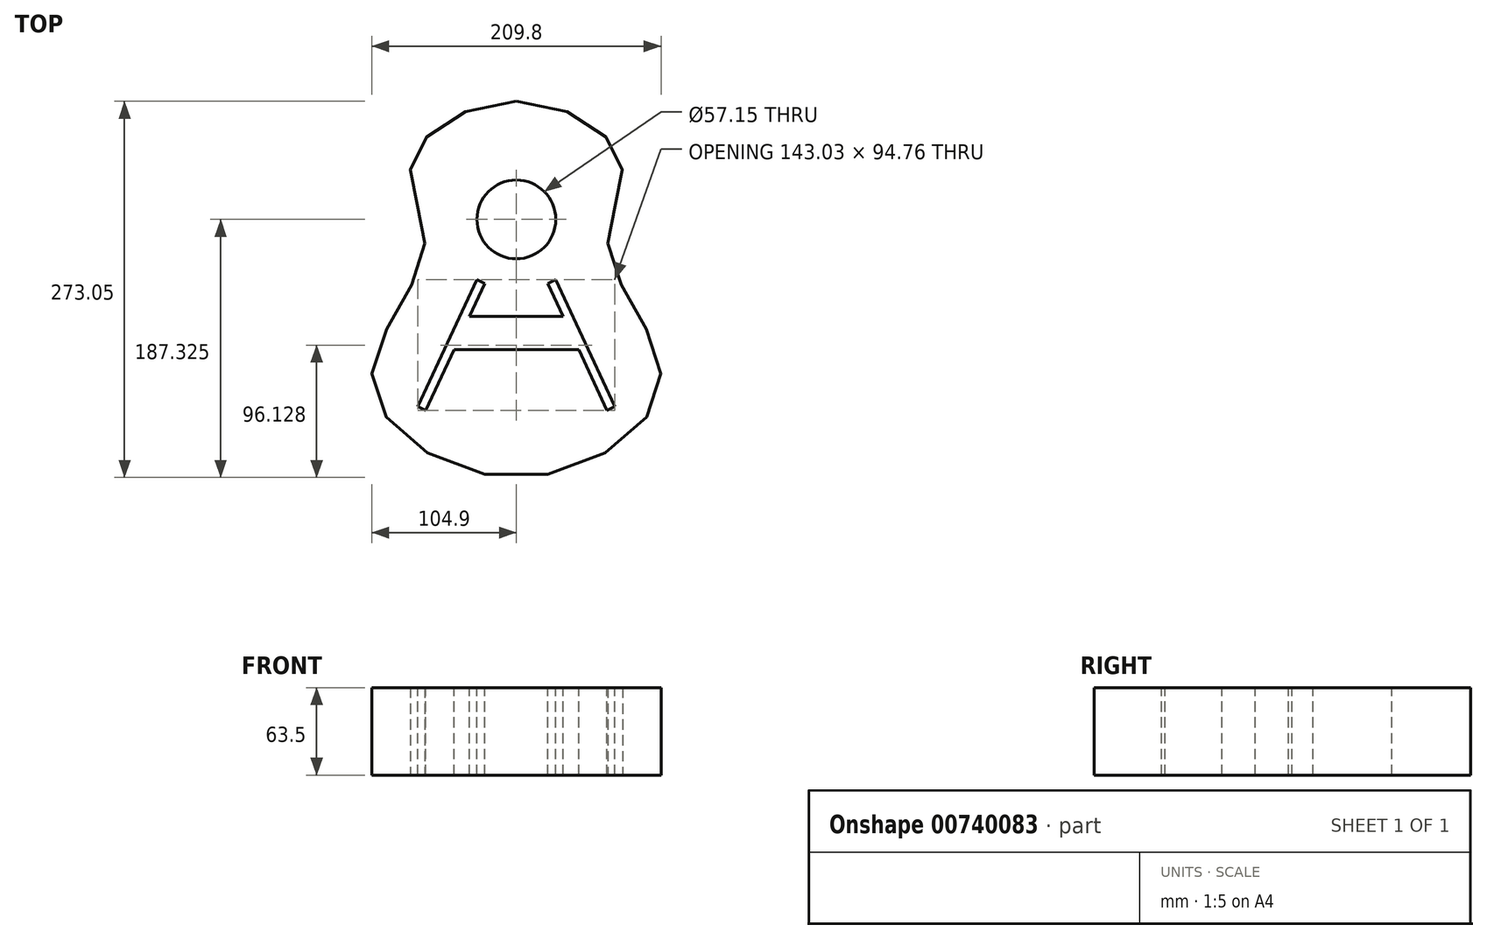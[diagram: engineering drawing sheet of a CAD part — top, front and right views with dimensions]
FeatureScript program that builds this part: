
annotation { "Feature Type Name" : "Feature", "Feature Type Description" : "" }
export const myFeature = defineFeature(function(context is Context, id is Id, definition is map)
    precondition{}
    {
        {
            var Q0;
            Q0=qCreatedBy(makeId("Top.planeOp"),FACE);
            var sketch = newSketch(context, id + "F0", { "sketchPlane" : qUnion([Q0])});
            skLineSegment(sketch, "E0", {"start": v(0, 63.5) * mm, "end": v(-76.2, 63.5) * mm, "construction": true});
            skLineSegment(sketch, "E1", {"start": v(-76.2, 63.5) * mm, "end": v(-66.67, 0) * mm, "construction": true});
            skLineSegment(sketch, "E2", {"start": v(-66.67, 0) * mm, "end": v(-104.78, -95.25) * mm, "construction": true});
            skLineSegment(sketch, "E3", {"start": v(-104.78, -95.25) * mm, "end": v(0, -95.25) * mm, "construction": true});
            skLineSegment(sketch, "E4", {"start": v(0, -95.25) * mm, "end": v(104.78, -95.25) * mm, "construction": true});
            skLineSegment(sketch, "E5", {"start": v(104.78, -95.25) * mm, "end": v(66.67, 0) * mm, "construction": true});
            skLineSegment(sketch, "E6", {"start": v(66.68, 0) * mm, "end": v(76.2, 63.5) * mm, "construction": true});
            skLineSegment(sketch, "E7", {"start": v(76.2, 63.5) * mm, "end": v(0, 63.5) * mm, "construction": true});
            skLineSegment(sketch, "E8", {"start": v(0, 107.95) * mm, "end": v(0, -165.1) * mm, "construction": true});
            skLineSegment(sketch, "E9", {"start": v(-66.68, 0) * mm, "end": v(66.68, 0) * mm, "construction": true});
            skFitSpline(sketch, "E10", {"points": [v(0, 107.95) * mm, v(-76.2, 63.5) * mm, v(-66.67, 0) * mm, v(-104.78, -95.25) * mm, v(0, -165.1) * mm, v(104.78, -95.25) * mm, v(66.68, 0) * mm, v(76.2, 63.5) * mm, v(0, 107.95) * mm]});
            skSolve(sketch);
        }
        {
            var Q0;
            Q0=qCreatedBy(makeId("Top.planeOp"),FACE);
            var sketch = newSketch(context, id + "F1", { "sketchPlane" : qUnion([Q0])});
            skPoint(sketch, "E11", {"position": v(0, 107.95) * mm});
            skPoint(sketch, "E12", {"position": v(76.2, 63.5) * mm});
            skPoint(sketch, "E13", {"position": v(66.68, 0) * mm});
            skPoint(sketch, "E14", {"position": v(104.78, -95.25) * mm});
            skPoint(sketch, "E15", {"position": v(0, -165.1) * mm});
            skPoint(sketch, "E16", {"position": v(-104.78, -95.25) * mm});
            skPoint(sketch, "E17", {"position": v(-66.68, 0) * mm});
            skPoint(sketch, "E18", {"position": v(-76.2, 63.5) * mm});
            skFitSpline(sketch, "E19", {"points": [v(0, 107.95) * mm, v(-76.2, 63.5) * mm, v(-66.68, 0) * mm, v(-104.78, -95.25) * mm, v(0, -165.1) * mm, v(104.78, -95.25) * mm, v(66.68, 0) * mm, v(76.2, 63.5) * mm, v(0, 107.95) * mm]});
            skFitSpline(sketch, "E20.0", {"points": [v(3.06, 98.39) * mm, v(0, 98.44) * mm, v(-3.06, 98.39) * mm, v(-7.14, 98.15) * mm, v(-12.24, 97.57) * mm, v(-18.3, 96.45) * mm, v(-26.22, 94.42) * mm, v(-35.7, 90.95) * mm, v(-44.24, 86.47) * mm, v(-50.29, 82.45) * mm, v(-54.38, 79.26) * mm, v(-57.97, 75.96) * mm, v(-61.01, 72.6) * mm, v(-63.48, 69.23) * mm, v(-65.03, 66.5) * mm, v(-65.97, 64.39) * mm, v(-66.43, 63.1) * mm, v(-66.73, 62.1) * mm, v(-66.92, 61.36) * mm, v(-67.08, 60.62) * mm, v(-67.26, 59.63) * mm, v(-67.4, 58.35) * mm, v(-67.5, 56.23) * mm, v(-67.35, 53.39) * mm, v(-66.76, 49.65) * mm, v(-65.8, 45.6) * mm, v(-64.56, 41.27) * mm, v(-63.1, 36.66) * mm, v(-61.55, 31.8) * mm, v(-60, 26.7) * mm, v(-58.6, 21.32) * mm, v(-57.48, 15.67) * mm, v(-56.9, 10.72) * mm, v(-56.74, 6.63) * mm, v(-56.78, 3.49) * mm, v(-57.01, 0.3) * mm, v(-57.46, -2.95) * mm, v(-58.1, -6.15) * mm, v(-59.18, -10.35) * mm, v(-60.91, -15.5) * mm, v(-63.46, -21.57) * mm, v(-66.37, -27.53) * mm, v(-69.53, -33.42) * mm, v(-72.86, -39.25) * mm, v(-77.38, -46.95) * mm, v(-82.97, -56.44) * mm, v(-87.88, -65.68) * mm, v(-91.05, -72.83) * mm, v(-92.98, -78.04) * mm, v(-94.39, -83.06) * mm, v(-95.23, -87.86) * mm, v(-95.42, -91.3) * mm, v(-95.35, -93.53) * mm, v(-95.28, -94.63) * mm, v(-95.16, -95.74) * mm, v(-94.96, -97.22) * mm, v(-94.6, -99.08) * mm, v(-93.81, -102.1) * mm, v(-92.42, -105.91) * mm, v(-90.09, -110.54) * mm, v(-86.12, -116.73) * mm, v(-79.6, -124.35) * mm, v(-69.59, -132.9) * mm, v(-57.74, -140.53) * mm, v(-44.46, -146.9) * mm, v(-32.52, -150.95) * mm, v(-22.66, -153.3) * mm, v(-15.15, -154.6) * mm, v(-8.84, -155.26) * mm, v(-3.78, -155.53) * mm, v(0, -155.6) * mm, v(3.78, -155.53) * mm, v(8.84, -155.26) * mm, v(15.15, -154.6) * mm, v(22.66, -153.3) * mm, v(32.52, -150.95) * mm, v(44.46, -146.9) * mm, v(57.74, -140.53) * mm, v(69.59, -132.9) * mm, v(79.6, -124.35) * mm, v(86.12, -116.73) * mm, v(90.09, -110.54) * mm, v(92.42, -105.91) * mm, v(93.81, -102.1) * mm, v(94.6, -99.08) * mm, v(94.96, -97.22) * mm, v(95.16, -95.74) * mm, v(95.28, -94.63) * mm, v(95.35, -93.53) * mm, v(95.42, -91.3) * mm, v(95.23, -87.86) * mm, v(94.39, -83.06) * mm, v(92.98, -78.04) * mm, v(91.05, -72.83) * mm, v(87.88, -65.68) * mm, v(82.97, -56.44) * mm, v(77.38, -46.95) * mm, v(72.86, -39.25) * mm, v(69.53, -33.42) * mm, v(66.37, -27.53) * mm, v(63.46, -21.57) * mm, v(60.91, -15.5) * mm, v(59.18, -10.35) * mm, v(58.1, -6.15) * mm, v(57.46, -2.95) * mm, v(57.01, 0.3) * mm, v(56.78, 3.49) * mm, v(56.74, 6.63) * mm, v(56.9, 10.72) * mm, v(57.48, 15.67) * mm, v(58.6, 21.32) * mm, v(60, 26.7) * mm, v(61.55, 31.8) * mm, v(63.1, 36.66) * mm, v(64.56, 41.27) * mm, v(65.8, 45.6) * mm, v(66.76, 49.65) * mm, v(67.35, 53.39) * mm, v(67.5, 56.23) * mm, v(67.4, 58.35) * mm, v(67.26, 59.63) * mm, v(67.08, 60.62) * mm, v(66.92, 61.36) * mm, v(66.73, 62.1) * mm, v(66.43, 63.1) * mm, v(65.97, 64.39) * mm, v(65.03, 66.5) * mm, v(63.48, 69.23) * mm, v(61.01, 72.6) * mm, v(57.97, 75.96) * mm, v(54.38, 79.26) * mm, v(50.29, 82.45) * mm, v(44.24, 86.47) * mm, v(35.7, 90.95) * mm, v(26.22, 94.42) * mm, v(18.3, 96.45) * mm, v(12.24, 97.57) * mm, v(7.14, 98.15) * mm, v(3.06, 98.39) * mm, v(0, 98.44) * mm, v(-3.06, 98.39) * mm, v(3.06, 98.39) * mm]});
            skCircle(sketch, "E21", {"center": v(0, 22.23) * mm, "radius": 28.58 * mm});
            skLineSegment(sketch, "E22", {"start": v(-22.23, -139.7) * mm, "end": v(22.23, -139.7) * mm});
            skPoint(sketch, "E23", {"position": v(0, -139.7) * mm});
            skLineSegment(sketch, "E24", {"start": v(-22.23, -139.7) * mm, "end": v(-22.23, -163.01) * mm});
            skLineSegment(sketch, "E25", {"start": v(22.23, -139.7) * mm, "end": v(22.23, -163.01) * mm});
            skLineSegment(sketch, "E26", {"start": v(-22.23, -163.01) * mm, "end": v(0, -163.01) * mm, "construction": true});
            skLineSegment(sketch, "E27", {"start": v(0, -163.01) * mm, "end": v(22.23, -163.01) * mm, "construction": true});
            skLineSegment(sketch, "E28", {"start": v(-25.4, 82.55) * mm, "end": v(25.4, 82.55) * mm});
            skLineSegment(sketch, "E29", {"start": v(25.4, 82.55) * mm, "end": v(25.4, 104.43) * mm});
            skLineSegment(sketch, "E30", {"start": v(-25.4, 82.55) * mm, "end": v(-25.4, 104.43) * mm});
            skPoint(sketch, "E31", {"position": v(0, 82.55) * mm});
            skLineSegment(sketch, "E32", {"start": v(-25.4, 104.43) * mm, "end": v(0, 104.43) * mm, "construction": true});
            skLineSegment(sketch, "E33", {"start": v(0, 104.43) * mm, "end": v(25.4, 104.43) * mm, "construction": true});
            skFitSpline(sketch, "E34.0", {"points": [v(6.6, 104.6) * mm, v(0, 104.86) * mm, v(-6.6, 104.6) * mm, v(-15.37, 103.6) * mm, v(-26.12, 101.22) * mm, v(-38.27, 96.77) * mm, v(-49.27, 91.01) * mm, v(-57.14, 85.35) * mm, v(-62.47, 80.45) * mm, v(-65.92, 76.63) * mm, v(-68.8, 72.72) * mm, v(-71.06, 68.76) * mm, v(-72.4, 65.45) * mm, v(-73.13, 62.82) * mm, v(-73.64, 60.18) * mm, v(-73.9, 56.83) * mm, v(-73.67, 52.68) * mm, v(-72.99, 48.4) * mm, v(-71.6, 42.49) * mm, v(-69.18, 34.78) * mm, v(-66.56, 26.65) * mm, v(-64.8, 19.88) * mm, v(-63.76, 14.66) * mm, v(-63.24, 10.19) * mm, v(-63.09, 6.54) * mm, v(-63.13, 3.76) * mm, v(-63.33, 0.95) * mm, v(-63.72, -1.89) * mm, v(-64.3, -4.73) * mm, v(-65.26, -8.51) * mm, v(-66.85, -13.24) * mm, v(-69.24, -18.92) * mm, v(-72.02, -24.62) * mm, v(-76.1, -32.23) * mm, v(-81.7, -41.8) * mm, v(-88.49, -53.3) * mm, v(-94.58, -64.76) * mm, v(-98.5, -74.2) * mm, v(-100.58, -81.62) * mm, v(-101.55, -87.1) * mm, v(-101.8, -91.6) * mm, v(-101.63, -95.17) * mm, v(-101.2, -98.72) * mm, v(-100.2, -103.16) * mm, v(-98.25, -108.46) * mm, v(-95.6, -113.72) * mm, v(-91.18, -120.6) * mm, v(-84.08, -128.89) * mm, v(-73.37, -138.03) * mm, v(-60.84, -146.1) * mm, v(-46.86, -152.8) * mm, v(-31.8, -157.9) * mm, v(-18.69, -160.61) * mm, v(-8.03, -161.73) * mm, v(0, -162.02) * mm, v(8.03, -161.73) * mm, v(18.69, -160.61) * mm, v(31.8, -157.9) * mm, v(46.86, -152.8) * mm, v(60.84, -146.1) * mm, v(73.37, -138.03) * mm, v(84.08, -128.89) * mm, v(91.18, -120.6) * mm, v(95.6, -113.72) * mm, v(98.25, -108.46) * mm, v(100.2, -103.16) * mm, v(101.2, -98.72) * mm, v(101.63, -95.17) * mm, v(101.8, -91.6) * mm, v(101.55, -87.1) * mm, v(100.58, -81.62) * mm, v(98.5, -74.2) * mm, v(94.58, -64.76) * mm, v(88.49, -53.3) * mm, v(81.7, -41.8) * mm, v(76.1, -32.23) * mm, v(72.02, -24.62) * mm, v(69.24, -18.92) * mm, v(66.85, -13.24) * mm, v(65.26, -8.51) * mm, v(64.3, -4.73) * mm, v(63.72, -1.89) * mm, v(63.33, 0.95) * mm, v(63.13, 3.76) * mm, v(63.09, 6.54) * mm, v(63.24, 10.19) * mm, v(63.76, 14.66) * mm, v(64.8, 19.88) * mm, v(66.56, 26.65) * mm, v(69.18, 34.78) * mm, v(71.6, 42.49) * mm, v(72.99, 48.4) * mm, v(73.67, 52.68) * mm, v(73.9, 56.83) * mm, v(73.64, 60.18) * mm, v(73.13, 62.82) * mm, v(72.4, 65.45) * mm, v(71.06, 68.76) * mm, v(68.8, 72.72) * mm, v(65.92, 76.63) * mm, v(62.47, 80.45) * mm, v(57.14, 85.35) * mm, v(49.27, 91.01) * mm, v(38.27, 96.77) * mm, v(26.12, 101.22) * mm, v(15.37, 103.6) * mm, v(6.6, 104.6) * mm, v(0, 104.86) * mm, v(-6.6, 104.6) * mm, v(6.6, 104.6) * mm]});
            skLineSegment(sketch, "E35", {"start": v(-25.4, 450.85) * mm, "end": v(25.4, 450.85) * mm});
            skLineSegment(sketch, "E36", {"start": v(25.4, 450.85) * mm, "end": v(15.88, 323.85) * mm});
            skLineSegment(sketch, "E37", {"start": v(15.88, 323.85) * mm, "end": v(25.4, 104.43) * mm});
            skLineSegment(sketch, "E38", {"start": v(-25.4, 104.43) * mm, "end": v(-15.87, 323.85) * mm});
            skLineSegment(sketch, "E39", {"start": v(-15.87, 323.85) * mm, "end": v(-25.4, 450.85) * mm});
            skPoint(sketch, "E40", {"position": v(0, 450.85) * mm});
            skLineSegment(sketch, "E41", {"start": v(0, 450.85) * mm, "end": v(0, 107.95) * mm, "construction": true});
            skLineSegment(sketch, "E42", {"start": v(-15.87, 323.85) * mm, "end": v(0, 323.85) * mm});
            skLineSegment(sketch, "E43", {"start": v(0, 323.85) * mm, "end": v(15.88, 323.85) * mm});
            skArc(sketch, "E44", {"start": v(-9.53, 101.06) * mm, "mid": v(-12.7, 97.88) * mm, "end": v(-9.53, 94.7) * mm});
            skLineSegment(sketch, "E45", {"start": v(-9.53, 101.06) * mm, "end": v(-9.53, 94.7) * mm, "construction": true});
            skLineSegment(sketch, "E46", {"start": v(-9.53, 94.7) * mm, "end": v(0, 94.7) * mm});
            skArc(sketch, "E47", {"start": v(-9.53, 101.06) * mm, "mid": v(-6.73, 104.57) * mm, "end": v(-10.24, 107.37) * mm});
            skArc(sketch, "E48.MirrorCS", {"start": v(9.53, 101.06) * mm, "mid": v(6.73, 104.57) * mm, "end": v(10.24, 107.37) * mm});
            skArc(sketch, "E49.MirrorCS", {"start": v(9.53, 101.06) * mm, "mid": v(12.7, 97.88) * mm, "end": v(9.53, 94.7) * mm});
            skLineSegment(sketch, "E50.MirrorCS", {"start": v(9.53, 94.7) * mm, "end": v(0, 94.7) * mm});
            skLineSegment(sketch, "E51", {"start": v(-16.1, 106.52) * mm, "end": v(-16.1, 96.83) * mm});
            skLineSegment(sketch, "E52.MirrorCS", {"start": v(16.1, 106.52) * mm, "end": v(16.1, 96.83) * mm});
            skLineSegment(sketch, "E53", {"start": v(-38.1, -57.15) * mm, "end": v(38.1, -57.15) * mm});
            skPoint(sketch, "E54", {"position": v(0, -57.15) * mm});
            skLineSegment(sketch, "E55", {"start": v(-50.8, -50.8) * mm, "end": v(50.8, -50.8) * mm});
            skLineSegment(sketch, "E56", {"start": v(50.8, -50.8) * mm, "end": v(38.1, -69.85) * mm});
            skLineSegment(sketch, "E57", {"start": v(38.1, -69.85) * mm, "end": v(-38.1, -69.85) * mm});
            skLineSegment(sketch, "E58", {"start": v(-38.1, -69.85) * mm, "end": v(-50.8, -50.8) * mm});
            skPoint(sketch, "E59", {"position": v(0, -50.8) * mm});
            skLineSegment(sketch, "E60", {"start": v(-12.06, -154.9) * mm, "end": v(-12.06, -164.48) * mm});
            skLineSegment(sketch, "E61.MirrorCS", {"start": v(12.06, -154.9) * mm, "end": v(12.06, -164.48) * mm});
            skCircle(sketch, "E62", {"center": v(-9.53, 374.65) * mm, "radius": 3.18 * mm});
            skCircle(sketch, "E63", {"center": v(-9.53, 412.75) * mm, "radius": 3.18 * mm});
            skLineSegment(sketch, "E64", {"start": v(-9.53, 412.75) * mm, "end": v(-9.53, 374.65) * mm, "construction": true});
            skCircle(sketch, "E65.MirrorC", {"center": v(9.52, 412.75) * mm, "radius": 3.18 * mm});
            skCircle(sketch, "E66.MirrorC", {"center": v(9.52, 374.65) * mm, "radius": 3.18 * mm});
            skPoint(sketch, "E67", {"position": v(0, -69.85) * mm});
            skLineSegment(sketch, "E68", {"start": v(-38.1, -57.15) * mm, "end": v(-38.1, -60.32) * mm});
            skLineSegment(sketch, "E69", {"start": v(-38.1, -60.32) * mm, "end": v(38.1, -60.32) * mm});
            skLineSegment(sketch, "E70", {"start": v(38.1, -60.32) * mm, "end": v(38.1, -57.15) * mm});
            skLineSegment(sketch, "E71", {"start": v(-26.9, 69.85) * mm, "end": v(26.9, 69.85) * mm});
            skLineSegment(sketch, "E72", {"start": v(-25.4, 104.43) * mm, "end": v(-26.9, 69.85) * mm});
            skLineSegment(sketch, "E73", {"start": v(25.4, 104.43) * mm, "end": v(26.9, 69.85) * mm});
            skLineSegment(sketch, "E74", {"start": v(-23.04, 158.75) * mm, "end": v(23.04, 158.75) * mm});
            skCircle(sketch, "E75", {"center": v(-15.88, 88.9) * mm, "radius": 3.18 * mm});
            skCircle(sketch, "E76.MirrorC", {"center": v(15.88, 88.9) * mm, "radius": 3.18 * mm});
            skCircle(sketch, "E77", {"center": v(-12.7, -146.05) * mm, "radius": 3.18 * mm});
            skLineSegment(sketch, "E78", {"start": v(0, -139.7) * mm, "end": v(0, -165.1) * mm, "construction": true});
            skCircle(sketch, "E79.MirrorC", {"center": v(12.7, -146.05) * mm, "radius": 3.18 * mm});
            skSolve(sketch);
        }
        {
            var Q0;
            Q0=qCreatedBy(makeId("Top.planeOp"),FACE);
            var sketch = newSketch(context, id + "F2", { "sketchPlane" : qUnion([Q0])});
            skPoint(sketch, "E80", {"position": v(0, 107.95) * mm});
            skPoint(sketch, "E81", {"position": v(-76.2, 63.5) * mm});
            skPoint(sketch, "E82", {"position": v(-66.68, 0) * mm});
            skPoint(sketch, "E83", {"position": v(0, -165.1) * mm});
            skPoint(sketch, "E84", {"position": v(104.78, -95.25) * mm});
            skPoint(sketch, "E85", {"position": v(66.68, 0) * mm});
            skPoint(sketch, "E86", {"position": v(76.2, 63.5) * mm});
            skPoint(sketch, "E87", {"position": v(-104.78, -95.25) * mm});
            skFitSpline(sketch, "E88", {"points": [v(0, 107.95) * mm, v(-76.2, 63.5) * mm, v(-66.68, 0) * mm, v(-104.78, -95.25) * mm, v(0, -165.1) * mm, v(104.78, -95.25) * mm, v(66.68, 0) * mm, v(76.2, 63.5) * mm, v(0, 107.95) * mm]});
            skCircle(sketch, "E89", {"center": v(0, 22.23) * mm, "radius": 28.58 * mm});
            skFitSpline(sketch, "E90.0", {"points": [v(6.6, 104.6) * mm, v(0, 104.86) * mm, v(-6.6, 104.6) * mm, v(-15.37, 103.6) * mm, v(-26.12, 101.22) * mm, v(-38.27, 96.77) * mm, v(-49.27, 91.01) * mm, v(-57.14, 85.35) * mm, v(-62.47, 80.45) * mm, v(-65.92, 76.63) * mm, v(-68.8, 72.72) * mm, v(-71.06, 68.76) * mm, v(-72.4, 65.45) * mm, v(-73.13, 62.82) * mm, v(-73.64, 60.18) * mm, v(-73.9, 56.83) * mm, v(-73.67, 52.68) * mm, v(-72.99, 48.4) * mm, v(-71.6, 42.49) * mm, v(-69.18, 34.78) * mm, v(-66.56, 26.65) * mm, v(-64.8, 19.88) * mm, v(-63.76, 14.66) * mm, v(-63.24, 10.19) * mm, v(-63.09, 6.54) * mm, v(-63.13, 3.76) * mm, v(-63.33, 0.95) * mm, v(-63.72, -1.89) * mm, v(-64.3, -4.73) * mm, v(-65.26, -8.51) * mm, v(-66.85, -13.24) * mm, v(-69.24, -18.92) * mm, v(-72.02, -24.62) * mm, v(-76.1, -32.23) * mm, v(-81.7, -41.8) * mm, v(-88.49, -53.3) * mm, v(-94.58, -64.76) * mm, v(-98.5, -74.2) * mm, v(-100.58, -81.62) * mm, v(-101.55, -87.1) * mm, v(-101.8, -91.6) * mm, v(-101.63, -95.17) * mm, v(-101.2, -98.72) * mm, v(-100.2, -103.16) * mm, v(-98.25, -108.46) * mm, v(-95.6, -113.72) * mm, v(-91.18, -120.6) * mm, v(-84.08, -128.89) * mm, v(-73.37, -138.03) * mm, v(-60.84, -146.1) * mm, v(-46.86, -152.8) * mm, v(-31.8, -157.9) * mm, v(-18.69, -160.61) * mm, v(-8.03, -161.73) * mm, v(0, -162.02) * mm, v(8.03, -161.73) * mm, v(18.69, -160.61) * mm, v(31.8, -157.9) * mm, v(46.86, -152.8) * mm, v(60.84, -146.1) * mm, v(73.37, -138.03) * mm, v(84.08, -128.89) * mm, v(91.18, -120.6) * mm, v(95.6, -113.72) * mm, v(98.25, -108.46) * mm, v(100.2, -103.16) * mm, v(101.2, -98.72) * mm, v(101.63, -95.17) * mm, v(101.8, -91.6) * mm, v(101.55, -87.1) * mm, v(100.58, -81.62) * mm, v(98.5, -74.2) * mm, v(94.58, -64.76) * mm, v(88.49, -53.3) * mm, v(81.7, -41.8) * mm, v(76.1, -32.23) * mm, v(72.02, -24.62) * mm, v(69.24, -18.92) * mm, v(66.85, -13.24) * mm, v(65.26, -8.51) * mm, v(64.3, -4.73) * mm, v(63.72, -1.89) * mm, v(63.33, 0.95) * mm, v(63.13, 3.76) * mm, v(63.09, 6.54) * mm, v(63.24, 10.19) * mm, v(63.76, 14.66) * mm, v(64.8, 19.88) * mm, v(66.56, 26.65) * mm, v(69.18, 34.78) * mm, v(71.6, 42.49) * mm, v(72.99, 48.4) * mm, v(73.67, 52.68) * mm, v(73.9, 56.83) * mm, v(73.64, 60.18) * mm, v(73.13, 62.82) * mm, v(72.4, 65.45) * mm, v(71.06, 68.76) * mm, v(68.8, 72.72) * mm, v(65.92, 76.63) * mm, v(62.47, 80.45) * mm, v(57.14, 85.35) * mm, v(49.27, 91.01) * mm, v(38.27, 96.77) * mm, v(26.12, 101.22) * mm, v(15.37, 103.6) * mm, v(6.6, 104.6) * mm, v(0, 104.86) * mm, v(-6.6, 104.6) * mm, v(6.6, 104.6) * mm]});
            skLineSegment(sketch, "E91", {"start": v(-72.93, 63.5) * mm, "end": v(72.93, 63.5) * mm});
            skLineSegment(sketch, "E92", {"start": v(-73.8, 57.15) * mm, "end": v(73.8, 57.15) * mm});
            skLineSegment(sketch, "E93", {"start": v(-66.73, -12.7) * mm, "end": v(66.73, -12.7) * mm});
            skLineSegment(sketch, "E94", {"start": v(-69.36, -19.05) * mm, "end": v(69.36, -19.05) * mm});
            skLineSegment(sketch, "E95", {"start": v(-28.58, 22.23) * mm, "end": v(28.58, 22.23) * mm, "construction": true});
            skFitSpline(sketch, "E96.0", {"points": [v(3.06, 98.39) * mm, v(0, 98.44) * mm, v(-3.06, 98.39) * mm, v(-7.14, 98.15) * mm, v(-12.24, 97.57) * mm, v(-18.3, 96.45) * mm, v(-26.22, 94.42) * mm, v(-35.7, 90.95) * mm, v(-44.24, 86.47) * mm, v(-50.29, 82.45) * mm, v(-54.38, 79.26) * mm, v(-57.97, 75.96) * mm, v(-61.01, 72.6) * mm, v(-63.48, 69.23) * mm, v(-65.03, 66.5) * mm, v(-65.97, 64.39) * mm, v(-66.43, 63.1) * mm, v(-66.73, 62.1) * mm, v(-66.92, 61.36) * mm, v(-67.08, 60.62) * mm, v(-67.26, 59.63) * mm, v(-67.4, 58.35) * mm, v(-67.5, 56.23) * mm, v(-67.35, 53.39) * mm, v(-66.76, 49.65) * mm, v(-65.8, 45.6) * mm, v(-64.56, 41.27) * mm, v(-63.1, 36.66) * mm, v(-61.55, 31.8) * mm, v(-60, 26.7) * mm, v(-58.6, 21.32) * mm, v(-57.48, 15.67) * mm, v(-56.9, 10.72) * mm, v(-56.74, 6.63) * mm, v(-56.78, 3.49) * mm, v(-57.01, 0.3) * mm, v(-57.46, -2.95) * mm, v(-58.1, -6.15) * mm, v(-59.18, -10.35) * mm, v(-60.91, -15.5) * mm, v(-63.46, -21.57) * mm, v(-66.37, -27.53) * mm, v(-69.53, -33.42) * mm, v(-72.86, -39.25) * mm, v(-77.38, -46.95) * mm, v(-82.97, -56.44) * mm, v(-87.88, -65.68) * mm, v(-91.05, -72.83) * mm, v(-92.98, -78.04) * mm, v(-94.39, -83.06) * mm, v(-95.23, -87.86) * mm, v(-95.42, -91.3) * mm, v(-95.35, -93.53) * mm, v(-95.28, -94.63) * mm, v(-95.16, -95.74) * mm, v(-94.96, -97.22) * mm, v(-94.6, -99.08) * mm, v(-93.81, -102.1) * mm, v(-92.42, -105.91) * mm, v(-90.09, -110.54) * mm, v(-86.12, -116.73) * mm, v(-79.6, -124.35) * mm, v(-69.59, -132.9) * mm, v(-57.74, -140.53) * mm, v(-44.46, -146.9) * mm, v(-32.52, -150.95) * mm, v(-22.66, -153.3) * mm, v(-15.15, -154.6) * mm, v(-8.84, -155.26) * mm, v(-3.78, -155.53) * mm, v(0, -155.6) * mm, v(3.78, -155.53) * mm, v(8.84, -155.26) * mm, v(15.15, -154.6) * mm, v(22.66, -153.3) * mm, v(32.52, -150.95) * mm, v(44.46, -146.9) * mm, v(57.74, -140.53) * mm, v(69.59, -132.9) * mm, v(79.6, -124.35) * mm, v(86.12, -116.73) * mm, v(90.09, -110.54) * mm, v(92.42, -105.91) * mm, v(93.81, -102.1) * mm, v(94.6, -99.08) * mm, v(94.96, -97.22) * mm, v(95.16, -95.74) * mm, v(95.28, -94.63) * mm, v(95.35, -93.53) * mm, v(95.42, -91.3) * mm, v(95.23, -87.86) * mm, v(94.39, -83.06) * mm, v(92.98, -78.04) * mm, v(91.05, -72.83) * mm, v(87.88, -65.68) * mm, v(82.97, -56.44) * mm, v(77.38, -46.95) * mm, v(72.86, -39.25) * mm, v(69.53, -33.42) * mm, v(66.37, -27.53) * mm, v(63.46, -21.57) * mm, v(60.91, -15.5) * mm, v(59.18, -10.35) * mm, v(58.1, -6.15) * mm, v(57.46, -2.95) * mm, v(57.01, 0.3) * mm, v(56.78, 3.49) * mm, v(56.74, 6.63) * mm, v(56.9, 10.72) * mm, v(57.48, 15.67) * mm, v(58.6, 21.32) * mm, v(60, 26.7) * mm, v(61.55, 31.8) * mm, v(63.1, 36.66) * mm, v(64.56, 41.27) * mm, v(65.8, 45.6) * mm, v(66.76, 49.65) * mm, v(67.35, 53.39) * mm, v(67.5, 56.23) * mm, v(67.4, 58.35) * mm, v(67.26, 59.63) * mm, v(67.08, 60.62) * mm, v(66.92, 61.36) * mm, v(66.73, 62.1) * mm, v(66.43, 63.1) * mm, v(65.97, 64.39) * mm, v(65.03, 66.5) * mm, v(63.48, 69.23) * mm, v(61.01, 72.6) * mm, v(57.97, 75.96) * mm, v(54.38, 79.26) * mm, v(50.29, 82.45) * mm, v(44.24, 86.47) * mm, v(35.7, 90.95) * mm, v(26.22, 94.42) * mm, v(18.3, 96.45) * mm, v(12.24, 97.57) * mm, v(7.14, 98.15) * mm, v(3.06, 98.39) * mm, v(0, 98.44) * mm, v(-3.06, 98.39) * mm, v(3.06, 98.39) * mm]});
            skLineSegment(sketch, "E97", {"start": v(-28.58, -21.59) * mm, "end": v(-71.51, -113.67) * mm});
            skLineSegment(sketch, "E98", {"start": v(-71.51, -113.67) * mm, "end": v(-65.76, -116.35) * mm});
            skLineSegment(sketch, "E99", {"start": v(-65.76, -116.35) * mm, "end": v(-22.82, -24.27) * mm});
            skLineSegment(sketch, "E100", {"start": v(-22.82, -24.27) * mm, "end": v(-28.58, -21.59) * mm});
            skLineSegment(sketch, "E101.MirrorCS", {"start": v(28.57, -21.59) * mm, "end": v(71.51, -113.67) * mm});
            skLineSegment(sketch, "E102.MirrorCS", {"start": v(22.82, -24.27) * mm, "end": v(28.58, -21.59) * mm});
            skLineSegment(sketch, "E103.MirrorCS", {"start": v(65.76, -116.35) * mm, "end": v(22.82, -24.27) * mm});
            skLineSegment(sketch, "E104.MirrorCS", {"start": v(71.51, -113.67) * mm, "end": v(65.76, -116.35) * mm});
            skLineSegment(sketch, "E105", {"start": v(-34, -48.26) * mm, "end": v(34, -48.26) * mm});
            skLineSegment(sketch, "E106", {"start": v(-45.26, -72.39) * mm, "end": v(45.26, -72.39) * mm});
            skLineSegment(sketch, "E107", {"start": v(209.55, 63.5) * mm, "end": v(357.15, 63.5) * mm, "construction": true});
            skArc(sketch, "E108", {"start": v(357.15, 63.5) * mm, "mid": v(283.35, 64.4) * mm, "end": v(209.55, 63.5) * mm});
            skLineSegment(sketch, "E109", {"start": v(209.55, 63.5) * mm, "end": v(209.55, 51.7) * mm});
            skLineSegment(sketch, "E110", {"start": v(209.55, 51.7) * mm, "end": v(357.15, 51.7) * mm});
            skLineSegment(sketch, "E111", {"start": v(357.15, 51.7) * mm, "end": v(357.15, 63.5) * mm});
            skLineSegment(sketch, "E112", {"start": v(209.55, -12.7) * mm, "end": v(348.27, -12.7) * mm, "construction": true});
            skArc(sketch, "E113", {"start": v(348.27, -12.7) * mm, "mid": v(278.91, -11.91) * mm, "end": v(209.55, -12.7) * mm});
            skLineSegment(sketch, "E114", {"start": v(209.55, -12.7) * mm, "end": v(209.55, -24.61) * mm});
            skLineSegment(sketch, "E115", {"start": v(209.55, -24.61) * mm, "end": v(348.27, -24.61) * mm});
            skLineSegment(sketch, "E116", {"start": v(348.27, -24.61) * mm, "end": v(348.27, -12.7) * mm});
            skLineSegment(sketch, "E117", {"start": v(209.55, -82.97) * mm, "end": v(311.15, -82.97) * mm, "construction": true});
            skArc(sketch, "E118", {"start": v(311.15, -82.97) * mm, "mid": v(260.35, -82.55) * mm, "end": v(209.55, -82.97) * mm});
            skLineSegment(sketch, "E119", {"start": v(209.55, -82.97) * mm, "end": v(209.55, -95.25) * mm});
            skLineSegment(sketch, "E120", {"start": v(209.55, -95.25) * mm, "end": v(311.15, -95.25) * mm});
            skLineSegment(sketch, "E121", {"start": v(311.15, -95.25) * mm, "end": v(311.15, -82.97) * mm});
            skSolve(sketch);
        }
        {
            var Q0;
            Q0=qCreatedBy(makeId("Right.planeOp"),FACE);
            var sketch = newSketch(context, id + "F3", { "sketchPlane" : qUnion([Q0])});
            skLineSegment(sketch, "E122", {"start": v(107.95, 0) * mm, "end": v(107.95, -63.5) * mm, "construction": true});
            skLineSegment(sketch, "E123", {"start": v(107.95, -63.5) * mm, "end": v(-165.1, -63.5) * mm, "construction": true});
            skLineSegment(sketch, "E124", {"start": v(-165.1, -63.5) * mm, "end": v(-165.1, 0) * mm, "construction": true});
            skSolve(sketch);
        }
        {
            var Q0;
            Q0=sQuery(id+"F3.wireOp",EDGE,"E123");
            cPlane(context, id + "F4", {"entities" : qUnion([Q0]), "cplaneType" : CPlaneType.LINE_ANGLE, "offset" : 25.4 * mm, "angle" : 0 * degree, "width" : 152.4 * mm, "height" : 152.4 * mm});
        }
        {
            var Q0;
            Q0=makeQuery(id+"F2.imprint","IMPRINT",FACE,{"disambiguationData":[TD([[makeQuery(id+"F2.imprint","IMPRINT",EDGE,{"derivedFrom":sQuery(id+"F2.wireOp",EDGE,"E88")}),1.0]])]});
            var Q1;
            Q1=qCreatedBy(id+"F4.planeOp",FACE);
            extrude(context, id + "F5", {"entities" : qUnion([Q0]), "endBound" : BoundingType.UP_TO_SURFACE, "oppositeDirection" : true, "depth" : 12.7 * mm, "endBoundEntityFace" : qUnion([Q1]), "offsetDistance" : 25.4 * mm});
        }
    });
